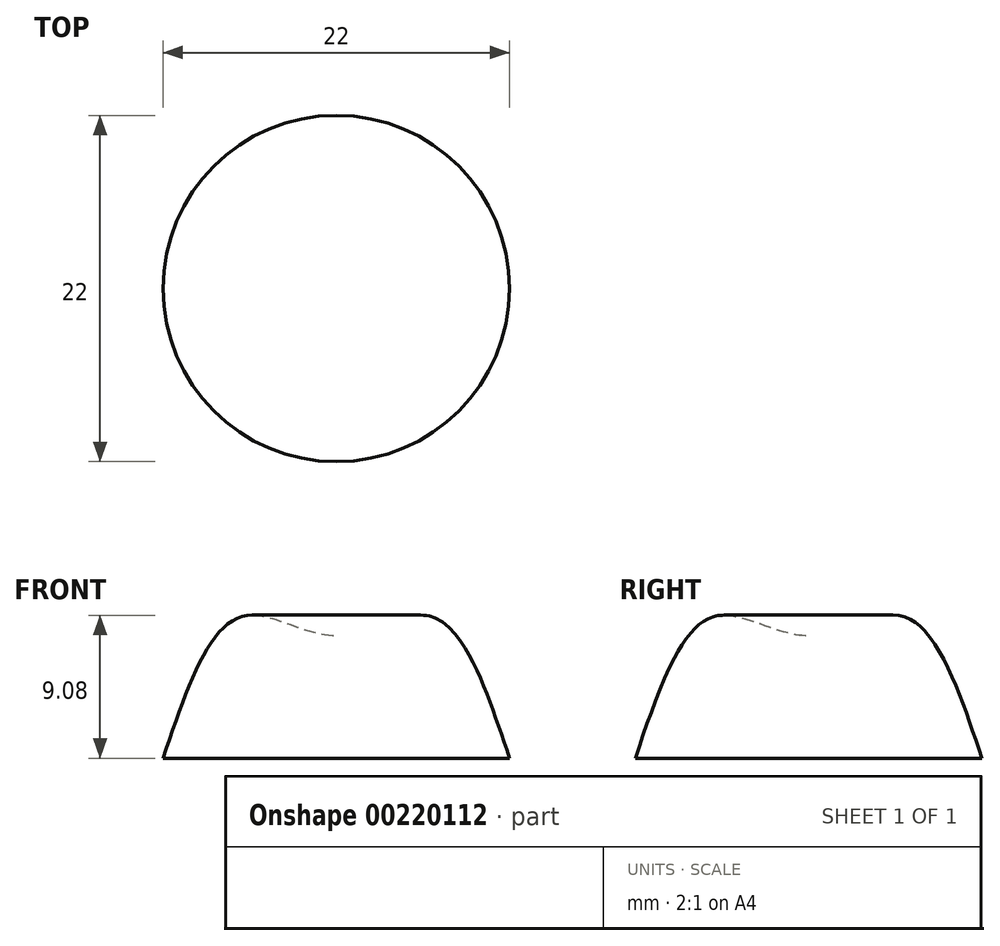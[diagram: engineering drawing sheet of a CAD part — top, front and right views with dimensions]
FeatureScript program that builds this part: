
annotation { "Feature Type Name" : "Feature", "Feature Type Description" : "" }
export const myFeature = defineFeature(function(context is Context, id is Id, definition is map)
    precondition{}
    {
        {
            var Q0;
            Q0=qCreatedBy(makeId("Top.planeOp"),FACE);
            cPlane(context, id + "F0", {"entities" : qUnion([Q0]), "cplaneType" : CPlaneType.OFFSET, "offset" : 9 * mm, "width" : 150 * mm, "height" : 150 * mm});
        }
        {
            var Q0;
            Q0=qCreatedBy(id+"F0.planeOp",FACE);
            cPlane(context, id + "F1", {"entities" : qUnion([Q0]), "cplaneType" : CPlaneType.OFFSET, "offset" : 2.5 * mm, "oppositeDirection" : true, "width" : 150 * mm, "height" : 150 * mm});
        }
        {
            var Q0;
            Q0=qCreatedBy(makeId("Top.planeOp"),FACE);
            var sketch = newSketch(context, id + "F2", { "sketchPlane" : qUnion([Q0])});
            skCircle(sketch, "E0", {"center": v(0, 0) * mm, "radius": 11 * mm});
            skSolve(sketch);
        }
        {
            var Q0;
            Q0=qCreatedBy(id+"F0.planeOp",FACE);
            var sketch = newSketch(context, id + "F3", { "sketchPlane" : qUnion([Q0])});
            skCircle(sketch, "E1", {"center": v(0, 0) * mm, "radius": 6 * mm});
            skSolve(sketch);
        }
        {
            var Q0;
            Q0=qCreatedBy(id+"F1.planeOp",FACE);
            var sketch = newSketch(context, id + "F4", { "sketchPlane" : qUnion([Q0])});
            skCircle(sketch, "E2", {"center": v(0, 0) * mm, "radius": 4 * mm});
            skSolve(sketch);
        }
        {
            var Q0;
            Q0=qCreatedBy(makeId("Front.planeOp"),FACE);
            var sketch = newSketch(context, id + "F5", { "sketchPlane" : qUnion([Q0])});
            skLineSegment(sketch, "E3.0", {"start": v(-11, 0) * mm, "end": v(0, 0) * mm, "construction": true});
            skLineSegment(sketch, "E4.0", {"start": v(-4, 6.5) * mm, "end": v(4, 6.5) * mm, "construction": true});
            skLineSegment(sketch, "E5.0", {"start": v(-6, 9) * mm, "end": v(4.6, 9) * mm, "construction": true});
            skFitSpline(sketch, "E6", {"points": [v(-11, 0) * mm, v(-6, 9) * mm, v(0, 7.8) * mm, v(6, 9) * mm, v(11, 0) * mm], "startDerivative": vector(14.93, 44.6) * mm, "endDerivative": vector(14.93, -44.6) * mm});
            skLineSegment(sketch, "E7", {"start": v(-11, 0) * mm, "end": v(0, 0) * mm});
            skLineSegment(sketch, "E8", {"start": v(0, 7.8) * mm, "end": v(0, 0) * mm});
            skLineSegment(sketch, "E9", {"start": v(0, 12.53) * mm, "end": v(0, 5.53) * mm, "construction": true});
            skPoint(sketch, "E9.startSnap0", {"position": v(0, 6.5) * mm});
            skSolve(sketch);
        }
        {
            var Q0;
            Q0 = qSketchRegion(id + "F5", true);
            var Q1;
            Q1=sQuery(id+"F5.wireOp",EDGE,"E9");
            revolve(context, id + "F6", {"entities" : qUnion([Q0]), "axis" : qUnion([Q1]), "revolveType" : RevolveType.FULL});
        }
    });
